# Revit family: 63__LF_UN_Emilux_Turijn-II_R17
name_source: partatom
category: Lighting Fixtures
revit_build: Autodesk Revit 2017 (Build: 20190508_0315(x64)
units: mm (PartAtom-declared; Revit-internal decimal feet)

## family parameters
Always vertical = Yes
Cut with Voids When Loaded = Yes
Light Source = Yes
Part Type = Normal
Room Calculation Point = No
Round Connector Dimension = Use Diameter
Shared = No
Work Plane-Based = No

## types (2) — shared parameters
Apparent Load = 36 VA
Assembly Code = 63.0
Color Filter = 16777215
Description = Turijn II LED 4050lm 4000K Ra80 (36W)
Dimming Lamp Color Temperature Shift = <None>
Emit Shape Visible in Rendering = No
IfcExportAs = IfcLightFixtureType
IfcExportType = POINTSOURCE
LED Driver = Yes
Lamp = LED
Manufacturer = EMILUX
Model = Turijn II
Tilt Angle = 90.00°
Type Comments = Turijn
URL = https://www.emilux.nl
Wattage Comments = 36W
zero-valued in all types: Cost

## per-type parameters (varying)
| type | Article Number | Emit from Rectangle Length | Emit from Rectangle Width | Photometric Web File |
| LED 4000lm 3000K Ra80 (36W) | 1TI12036840 | 1219 mm | 610 mm | Emilux TURIJN 30X120 36W 4000Lm 3000K Ra80_LDT.ies |
| LED 4050lm 4000K Ra80 (36W) | 1TII06036830 | 600 mm | 600 mm | Emilux TURIJN 30X120 36W 4050Lm 4000K Ra80_LDT.ies |

## geometry (parser evidence)
native form markers: Sweep x5
no freeform markers — native parametric forms only
